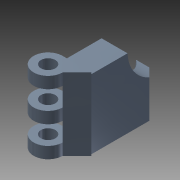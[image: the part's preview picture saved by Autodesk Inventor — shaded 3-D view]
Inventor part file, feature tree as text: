
AUTODESK INVENTOR PART (.ipt)
format: ipt  version: 2015 (Build 190159000, 159)  size: 185,344 bytes
history: native  units: mm
features: sketch x6, extrude x4, other x2, revolve x2, plane x1
ambient origin geometry x8: Origin, YZ Plane, XZ Plane, XY Plane, X Axis, Y Axis, Z Axis, Center Point
bodies: 实体1 (feature_tree)
feature tree (15):
  extrude  "拉伸1"  Depth=10.0mm
  plane  "工作平面1"
  other  "工作轴1"
  revolve  "旋转1"  [1 undecoded]
  extrude  "拉伸2"  Depth=10.0mm
  extrude  "拉伸3"  Depth=50.0mm TaperAngle=0.0deg
  extrude  "拉伸4"  Depth=14.0mm
  revolve  "旋转2"  Angle=90.0deg
  sketch  "草图1"  dims[d0=20.0mm d1=10.0mm]
  other  "工作点1"
  sketch  "草图3"  dims[d2=20.0mm d3=50.0mm]
  sketch  "草图4"  dims[d4=135.0deg d5=10.0mm]
  sketch  "草图5"  dims[d6=45.0deg d7=50.0mm d8=0.0mm]
  sketch  "草图6"  dims[d9=-25.0mm d13=14.0mm]
  sketch  "草图7"  dims[d14=25.0mm d15=90.0deg d16=2.0mm d17=2.0mm d18=50.0mm d19=0.0mm d20=1.0mm d21=1.0mm d22=48.0mm d23=0.0mm d24=50.0mm d25=50.0mm d26=60.0mm d27=20.0mm d28=0.0mm d29=13.0mm d30=13.0mm d31=8.0mm d32=8.0mm d33=8.0mm d34=90.0deg]
note: 1 required parameter value undecoded (feature->parameter linkage not recoverable at this tier; creation-order binding heuristic only, values carry confidence <= 0.55)
